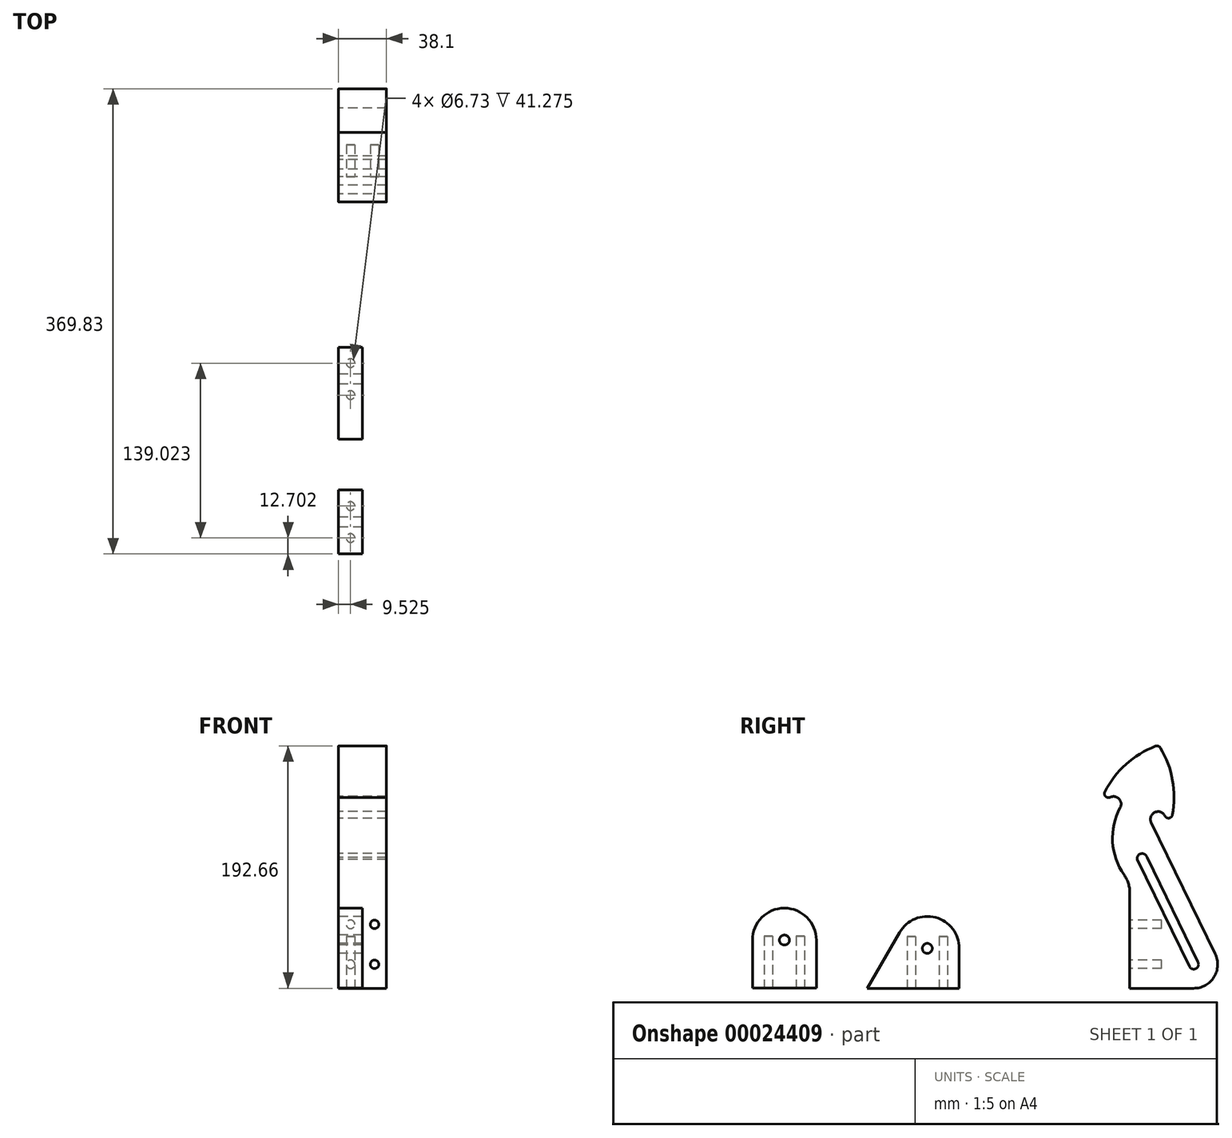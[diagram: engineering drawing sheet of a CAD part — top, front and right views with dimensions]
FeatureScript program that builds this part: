
annotation { "Feature Type Name" : "Feature", "Feature Type Description" : "" }
export const myFeature = defineFeature(function(context is Context, id is Id, definition is map)
    precondition{}
    {
        {
            var Q0;
            Q0=qCreatedBy(makeId("Right.planeOp"),FACE);
            var sketch = newSketch(context, id + "F0", { "sketchPlane" : qUnion([Q0])});
            skLineSegment(sketch, "E0", {"start": v(0, 0) * mm, "end": v(73.03, 0) * mm});
            skLineSegment(sketch, "E1", {"start": v(73.03, 0) * mm, "end": v(73.03, 31.75) * mm});
            skCircle(sketch, "E2", {"center": v(47.62, 31.75) * mm, "radius": 3.98 * mm});
            skArc(sketch, "E3", {"start": v(73.03, 31.75) * mm, "mid": v(54.2, 56.29) * mm, "end": v(25.62, 44.44) * mm});
            skLineSegment(sketch, "E4", {"start": v(73.03, 31.75) * mm, "end": v(47.62, 31.75) * mm, "construction": true});
            skLineSegment(sketch, "E5", {"start": v(0, 0) * mm, "end": v(25.62, 44.44) * mm});
            skSolve(sketch);
        }
        {
            var Q0;
            Q0 = qSketchRegion(id + "F0", true);
            extrude(context, id + "F1", {"entities" : qUnion([Q0]), "depth" : 19.05 * mm});
        }
        {
            var Q0;
            Q0=makeQuery(id+"F1.opExtrude","SWEPT_FACE",FACE,{"disambiguationData":[OSD([sQuery(id+"F0.wireOp",EDGE,"E0")])]});
            var sketch = newSketch(context, id + "F2", { "sketchPlane" : qUnion([Q0])});
            skCircle(sketch, "E6", {"center": v(9.53, -60.33) * mm, "radius": 3.37 * mm});
            skCircle(sketch, "E7", {"center": v(9.53, -34.92) * mm, "radius": 3.37 * mm});
            skLineSegment(sketch, "E8", {"start": v(9.53, -73.03) * mm, "end": v(9.53, 0) * mm, "construction": true});
            skSolve(sketch);
        }
        {
            var Q0;
            Q0 = qSketchRegion(id + "F2", true);
            extrude(context, id + "F3", {"entities" : qUnion([Q0]), "operationType" : NewBodyOperationType.REMOVE, "oppositeDirection" : true, "depth" : 41.27 * mm});
        }
        {
            var Q0;
            Q0=qCreatedBy(makeId("Right.planeOp"),FACE);
            var sketch = newSketch(context, id + "F4", { "sketchPlane" : qUnion([Q0])});
            skLineSegment(sketch, "E9", {"start": v(-91.4, 0.23) * mm, "end": v(-40.6, 0.23) * mm});
            skLineSegment(sketch, "E10", {"start": v(-40.6, 0.23) * mm, "end": v(-40.6, 38.33) * mm});
            skCircle(sketch, "E11", {"center": v(-66, 38.33) * mm, "radius": 3.98 * mm});
            skArc(sketch, "E12", {"start": v(-40.6, 38.33) * mm, "mid": v(-66, 63.73) * mm, "end": v(-91.4, 38.33) * mm});
            skLineSegment(sketch, "E13", {"start": v(-40.6, 38.33) * mm, "end": v(-66, 38.33) * mm, "construction": true});
            skLineSegment(sketch, "E14", {"start": v(-91.4, 0.23) * mm, "end": v(-91.4, 38.33) * mm});
            skSolve(sketch);
        }
        {
            var Q0;
            Q0=makeQuery(id+"F4.imprint","IMPRINT",FACE,{"disambiguationData":[TD([[makeQuery(id+"F4.imprint","IMPRINT",EDGE,{"derivedFrom":sQuery(id+"F4.wireOp",EDGE,"E9")}),1.0]])]});
            extrude(context, id + "F5", {"entities" : qUnion([Q0]), "depth" : 19.05 * mm});
        }
        {
            var Q0;
            Q0=makeQuery(id+"F5.opExtrude","SWEPT_FACE",FACE,{"disambiguationData":[OSD([sQuery(id+"F4.wireOp",EDGE,"E9")])]});
            var sketch = newSketch(context, id + "F6", { "sketchPlane" : qUnion([Q0])});
            skLineSegment(sketch, "E15", {"start": v(9.53, 91.4) * mm, "end": v(9.53, 40.6) * mm, "construction": true});
            skCircle(sketch, "E16", {"center": v(9.53, 78.7) * mm, "radius": 3.37 * mm});
            skCircle(sketch, "E17", {"center": v(9.53, 53.3) * mm, "radius": 3.37 * mm});
            skSolve(sketch);
        }
        {
            var Q0;
            Q0 = qSketchRegion(id + "F6", true);
            extrude(context, id + "F7", {"entities" : qUnion([Q0]), "operationType" : NewBodyOperationType.REMOVE, "oppositeDirection" : true, "depth" : 41.27 * mm});
        }
        {
            var Q0;
            Q0=qCreatedBy(makeId("Right.planeOp"),FACE);
            var sketch = newSketch(context, id + "F8", { "sketchPlane" : qUnion([Q0])});
            skLineSegment(sketch, "E18", {"start": v(208.58, 0) * mm, "end": v(208.58, 75.68) * mm});
            skLineSegment(sketch, "E19", {"start": v(208.58, 0) * mm, "end": v(259.38, 0) * mm});
            skArc(sketch, "E20", {"start": v(255.93, 17.37) * mm, "mid": v(261.06, 15.6) * mm, "end": v(262.83, 20.73) * mm});
            skArc(sketch, "E21", {"start": v(222.28, 103.88) * mm, "mid": v(217.62, 107.03) * mm, "end": v(214.47, 102.37) * mm});
            skArc(sketch, "E22", {"start": v(259.38, 0) * mm, "mid": v(275.54, 8.96) * mm, "end": v(276.5, 27.4) * mm});
            skLineSegment(sketch, "E23", {"start": v(218.38, 103.12) * mm, "end": v(259.38, 19.05) * mm, "construction": true});
            skLineSegment(sketch, "E24", {"start": v(222.28, 103.88) * mm, "end": v(262.83, 20.73) * mm});
            skLineSegment(sketch, "E25", {"start": v(214.47, 102.37) * mm, "end": v(255.93, 17.37) * mm});
            skLineSegment(sketch, "E26", {"start": v(276.5, 27.4) * mm, "end": v(225.61, 131.75) * mm});
            skArc(sketch, "E27", {"start": v(232.9, 191.12) * mm, "mid": v(231.2, 192.49) * mm, "end": v(229.02, 192.44) * mm});
            skArc(sketch, "E28", {"start": v(236.46, 137.04) * mm, "mid": v(239.74, 135.28) * mm, "end": v(242.44, 137.84) * mm});
            skArc(sketch, "E29", {"start": v(188.74, 156.13) * mm, "mid": v(189.3, 152.46) * mm, "end": v(192.98, 151.84) * mm});
            skArc(sketch, "E30", {"start": v(229.02, 192.44) * mm, "mid": v(205.54, 178) * mm, "end": v(188.74, 156.13) * mm});
            skArc(sketch, "E31.trimOffspring", {"start": v(242.44, 137.84) * mm, "mid": v(242.55, 165.36) * mm, "end": v(232.9, 191.12) * mm});
            skLineSegment(sketch, "E32", {"start": v(239.32, 138.43) * mm, "end": v(236.46, 137.04) * mm, "construction": true});
            skLineSegment(sketch, "E33", {"start": v(236.46, 137.04) * mm, "end": v(225.61, 131.75) * mm, "construction": true});
            skArc(sketch, "E34", {"start": v(236.46, 137.04) * mm, "mid": v(228.4, 139.82) * mm, "end": v(225.61, 131.75) * mm});
            skLineSegment(sketch, "E35", {"start": v(191.56, 154.69) * mm, "end": v(239.32, 138.43) * mm, "construction": true});
            skLineSegment(sketch, "E36", {"start": v(231.04, 134.4) * mm, "end": v(195.66, 146.44) * mm, "construction": true});
            skArc(sketch, "E37", {"start": v(200.97, 143.56) * mm, "mid": v(200, 150.63) * mm, "end": v(192.98, 151.84) * mm});
            skArc(sketch, "E38", {"start": v(200.97, 143.56) * mm, "mid": v(194.9, 116.47) * mm, "end": v(204, 90.23) * mm});
            skArc(sketch, "E39", {"start": v(208.58, 75.68) * mm, "mid": v(207.4, 83.3) * mm, "end": v(204, 90.23) * mm});
            skSolve(sketch);
        }
        {
            var Q0;
            Q0 = qSketchRegion(id + "F8", true);
            extrude(context, id + "F9", {"entities" : qUnion([Q0]), "depth" : 38.1 * mm});
        }
        {
            var Q0;
            Q0=makeQuery(id+"F9.opExtrude","SWEPT_FACE",FACE,{"disambiguationData":[OSD([sQuery(id+"F8.wireOp",EDGE,"E18")])]});
            var sketch = newSketch(context, id + "F10", { "sketchPlane" : qUnion([Q0])});
            skLineSegment(sketch, "E40", {"start": v(19.05, 0) * mm, "end": v(19.05, 75.68) * mm, "construction": true});
            skLineSegment(sketch, "E41", {"start": v(9.53, 19.05) * mm, "end": v(19.05, 19.05) * mm, "construction": true});
            skCircle(sketch, "E42", {"center": v(28.58, 19.05) * mm, "radius": 3.37 * mm});
            skCircle(sketch, "E43", {"center": v(9.53, 19.05) * mm, "radius": 3.37 * mm});
            skLineSegment(sketch, "E44", {"start": v(19.05, 19.05) * mm, "end": v(28.58, 19.05) * mm, "construction": true});
            skLineSegment(sketch, "E45", {"start": v(19.05, 50.8) * mm, "end": v(28.58, 50.8) * mm, "construction": true});
            skCircle(sketch, "E46", {"center": v(9.53, 50.8) * mm, "radius": 3.37 * mm});
            skCircle(sketch, "E47", {"center": v(28.58, 50.8) * mm, "radius": 3.37 * mm});
            skLineSegment(sketch, "E48", {"start": v(9.53, 50.8) * mm, "end": v(19.05, 50.8) * mm, "construction": true});
            skSolve(sketch);
        }
        {
            var Q0;
            Q0=makeQuery(id+"F10.imprint","IMPRINT",FACE,{"disambiguationData":[TD([[makeQuery(id+"F10.imprint","IMPRINT",EDGE,{"derivedFrom":sQuery(id+"F10.wireOp",EDGE,"E46")}),1.0]])]});
            var Q1;
            Q1=makeQuery(id+"F10.imprint","IMPRINT",FACE,{"disambiguationData":[TD([[makeQuery(id+"F10.imprint","IMPRINT",EDGE,{"derivedFrom":sQuery(id+"F10.wireOp",EDGE,"E47")}),1.0]])]});
            var Q2;
            Q2=makeQuery(id+"F10.imprint","IMPRINT",FACE,{"disambiguationData":[TD([[makeQuery(id+"F10.imprint","IMPRINT",EDGE,{"derivedFrom":sQuery(id+"F10.wireOp",EDGE,"E42")}),1.0]])]});
            var Q3;
            Q3=makeQuery(id+"F10.imprint","IMPRINT",FACE,{"disambiguationData":[TD([[makeQuery(id+"F10.imprint","IMPRINT",EDGE,{"derivedFrom":sQuery(id+"F10.wireOp",EDGE,"E43")}),1.0]])]});
            extrude(context, id + "F11", {"entities" : qUnion([Q0, Q1, Q2, Q3]), "operationType" : NewBodyOperationType.REMOVE, "oppositeDirection" : true, "depth" : 25.4 * mm});
        }
    });
